# Revit family: LS21 Circular Coffee Table
name_source: partatom
category: Furniture
revit_build: Autodesk Revit 2016 (Build: 20160525_1230(x64)
units: mm (PartAtom-declared; Revit-internal decimal feet)

## family parameters
Always vertical = Yes
Cut with Voids When Loaded = No
OmniClass Number = 23.40.20.00
OmniClass Title = General Furniture and Specialties
Room Calculation Point = No
Shared = No
Work Plane-Based = No

## types (2) — shared parameters
Frame = Gresham - Silver Metal
Manufacturer = Gresham Office Furniture
Range = LS21
Table Top = Gresham - Walnut
URL = www.gof.co.uk

## per-type parameters (varying)
| type | Diameter | Product Code |
| 700 Diameter | 700 mm  [stored 2.29659 ft] | LS21A1 |
| 800 Diameter | 800 mm  [stored 2.62467 ft] | LS21A2 |

note: [stored X ft] marks values corroborated as IEEE doubles in the binary element streams (Revit-internal decimal feet)

## geometry (parser evidence)
native form markers: Blend x4, Sweep x6
no freeform markers — native parametric forms only
